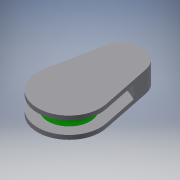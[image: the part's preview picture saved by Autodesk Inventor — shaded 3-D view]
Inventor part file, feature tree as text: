
AUTODESK INVENTOR PART (.ipt)
format: ipt  version: 2017 (Build 210142000, 142)  size: 144,896 bytes
history: native  units: mm
features: sketch x2, projected_geometry x2, extrude x1, revolve x1
ambient origin geometry x8: Origin, YZ Plane, XZ Plane, XY Plane, X Axis, Y Axis, Z Axis, Center Point
bodies: Solid1 (feature_tree)
feature tree (6):
  extrude  "Extrusion1"  Depth=50.0mm
  revolve  "Revolution1"  [1 undecoded]
  sketch  "Sketch1"  dims[d0=30.0mm d1=50.0mm]
  sketch  "Sketch2"  dims[d2=20.0mm d3=20.0mm d4=0.0mm d5=53.06342mm d6=40.0mm d7=12.0mm d8=90.0mm d9=90.0deg]
  projected_geometry  "Projected Loop1"
  projected_geometry  "Projected Loop2"
note: 1 required parameter value undecoded (feature->parameter linkage not recoverable at this tier; creation-order binding heuristic only, values carry confidence <= 0.55)
